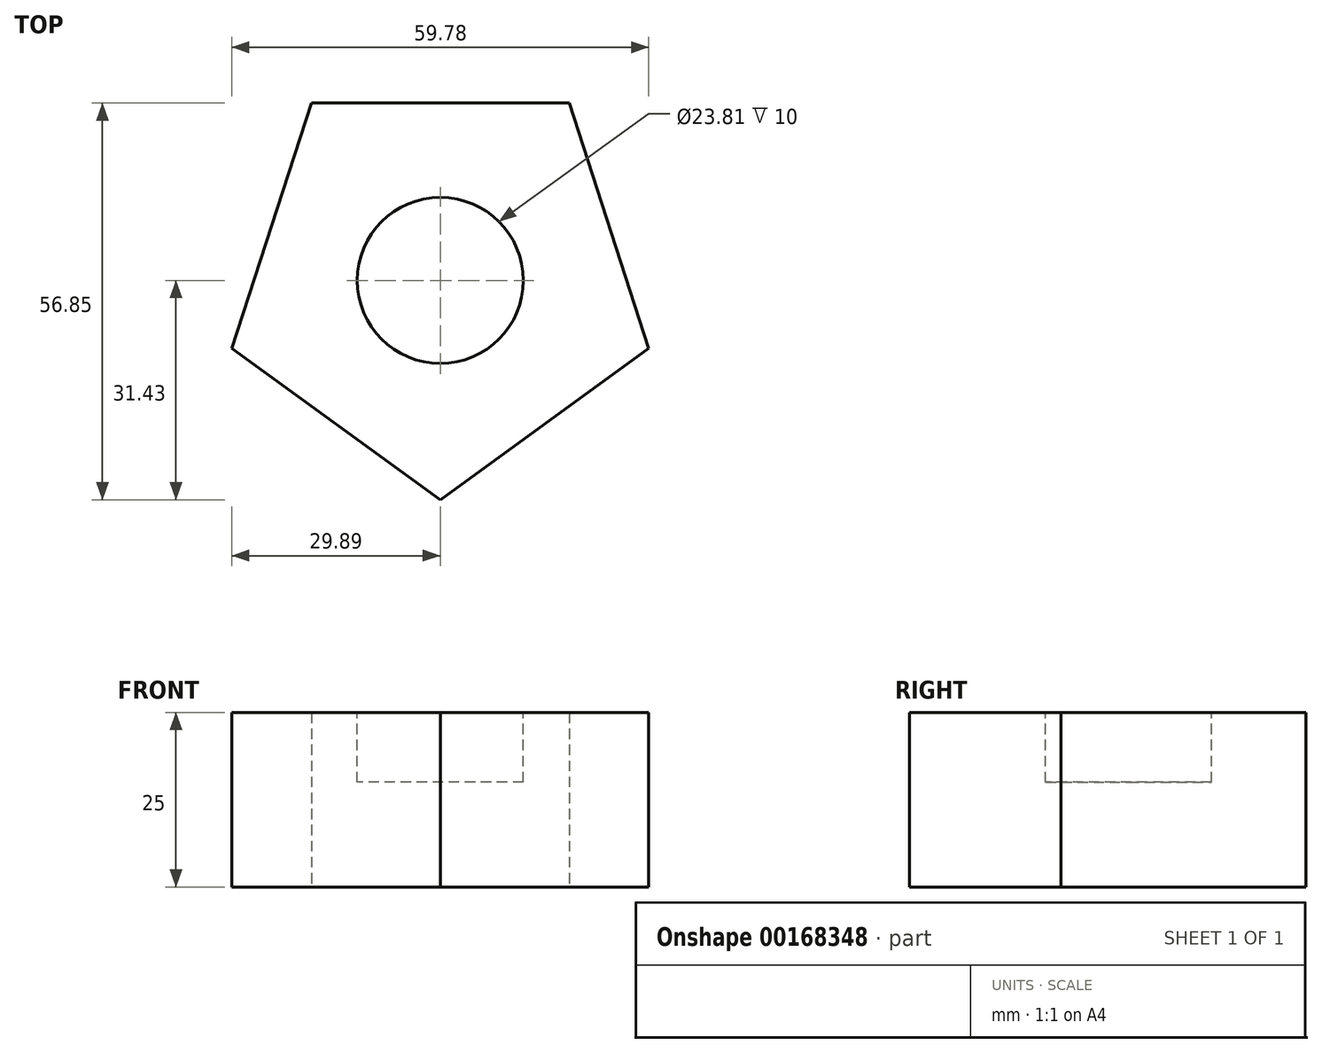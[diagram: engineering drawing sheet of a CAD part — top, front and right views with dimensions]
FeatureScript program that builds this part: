
annotation { "Feature Type Name" : "Feature", "Feature Type Description" : "" }
export const myFeature = defineFeature(function(context is Context, id is Id, definition is map)
    precondition{}
    {
        {
            var Q0;
            Q0=qCreatedBy(makeId("Top.planeOp"),FACE);
            var sketch = newSketch(context, id + "F0", { "sketchPlane" : qUnion([Q0])});
            skCircle(sketch, "E0.cCircle", {"center": v(0, 0) * mm, "radius": 25.42 * mm, "construction": true});
            skLineSegment(sketch, "E0.0", {"start": v(18.47, 25.42) * mm, "end": v(29.89, -9.71) * mm});
            skLineSegment(sketch, "E0.1", {"start": v(29.89, -9.71) * mm, "end": v(0, -31.43) * mm});
            skLineSegment(sketch, "E0.2", {"start": v(0, -31.43) * mm, "end": v(-29.89, -9.71) * mm});
            skLineSegment(sketch, "E0.3", {"start": v(-29.89, -9.71) * mm, "end": v(-18.47, 25.42) * mm});
            skLineSegment(sketch, "E0.4", {"start": v(-18.47, 25.42) * mm, "end": v(18.47, 25.42) * mm});
            skPoint(sketch, "E0.0.midPoint", {"position": v(24.18, 7.86) * mm});
            skSolve(sketch);
        }
        {
            var Q0;
            Q0 = qSketchRegion(id + "F0", true);
            extrude(context, id + "F1", {"entities" : qUnion([Q0]), "depth" : 25 * mm});
        }
        {
            var Q0;
            Q0=makeQuery(id+"F1.opExtrude","CAP_FACE",FACE,{"disambiguationData":[OSD([sQuery(id+"F0.wireOp",EDGE,"E0.0"),sQuery(id+"F0.wireOp",EDGE,"E0.1"),sQuery(id+"F0.wireOp",EDGE,"E0.2"),sQuery(id+"F0.wireOp",EDGE,"E0.3"),sQuery(id+"F0.wireOp",EDGE,"E0.4")])],"isStart":false});
            var sketch = newSketch(context, id + "F2", { "sketchPlane" : qUnion([Q0])});
            skCircle(sketch, "E1", {"center": v(0, 0) * mm, "radius": 11.9 * mm});
            skSolve(sketch);
        }
        {
            var Q0;
            Q0 = qSketchRegion(id + "F2", true);
            extrude(context, id + "F3", {"entities" : qUnion([Q0]), "operationType" : NewBodyOperationType.REMOVE, "oppositeDirection" : true, "depth" : 10 * mm});
        }
    });
